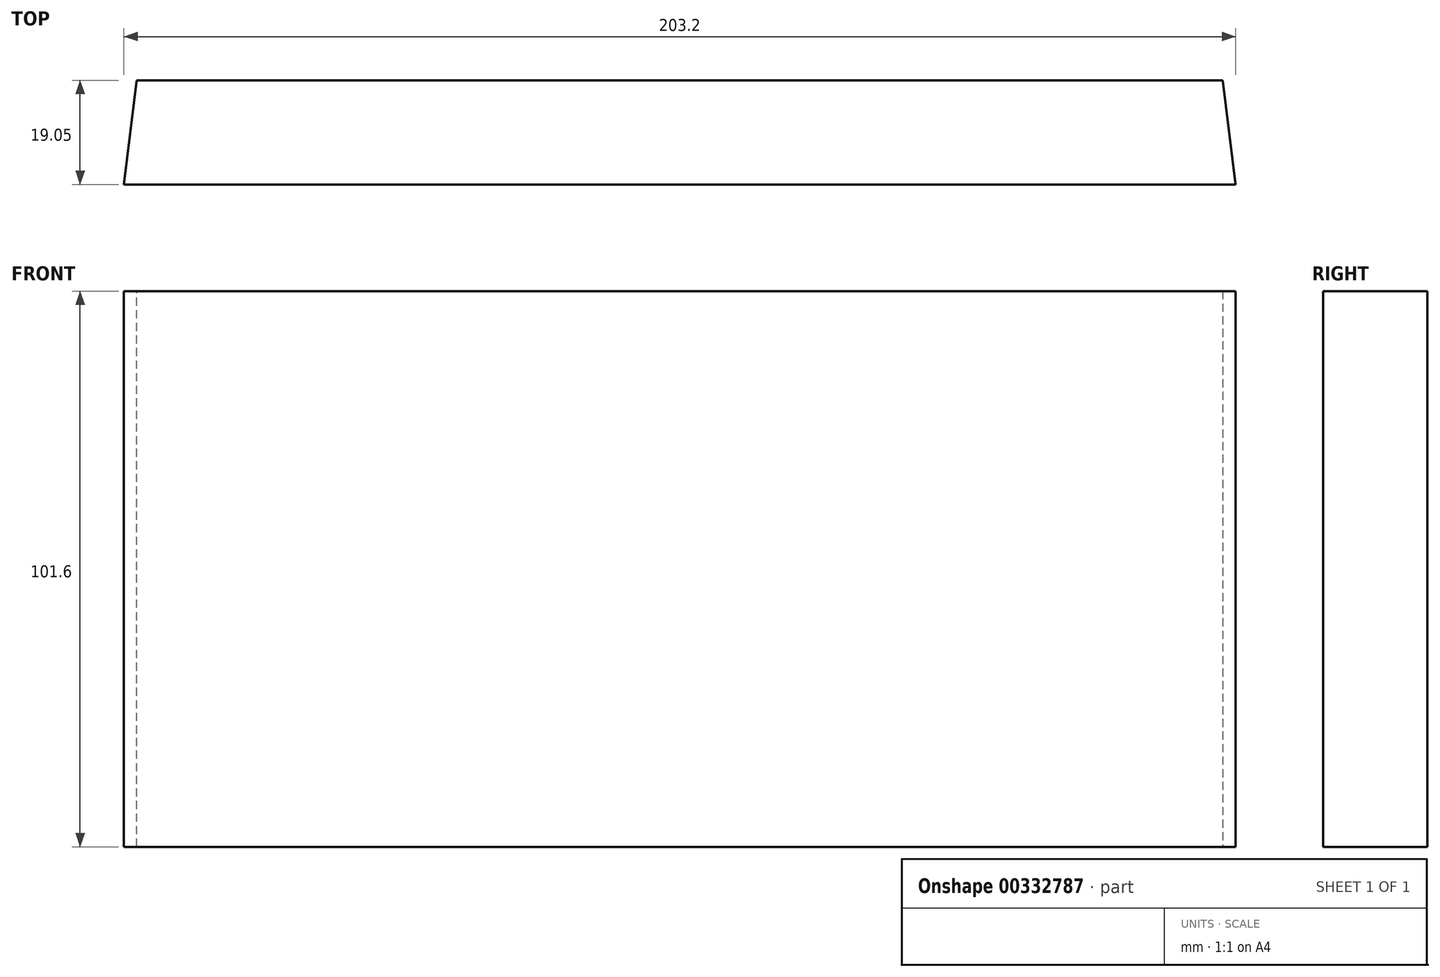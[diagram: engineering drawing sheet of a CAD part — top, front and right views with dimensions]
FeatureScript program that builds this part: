
annotation { "Feature Type Name" : "Feature", "Feature Type Description" : "" }
export const myFeature = defineFeature(function(context is Context, id is Id, definition is map)
    precondition{}
    {
        {
            var Q0;
            Q0=qCreatedBy(makeId("Front.planeOp"),FACE);
            var sketch = newSketch(context, id + "F0", { "sketchPlane" : qUnion([Q0])});
            skLineSegment(sketch, "E0.bottom", {"start": v(101.6, 50.8) * mm, "end": v(-101.6, 50.8) * mm});
            skLineSegment(sketch, "E0.top", {"start": v(101.6, -50.8) * mm, "end": v(-101.6, -50.8) * mm});
            skLineSegment(sketch, "E0.left", {"start": v(101.6, 50.8) * mm, "end": v(101.6, -50.8) * mm});
            skLineSegment(sketch, "E0.right", {"start": v(-101.6, 50.8) * mm, "end": v(-101.6, -50.8) * mm});
            skPoint(sketch, "E0.middle", {"position": v(0, 0) * mm});
            skSolve(sketch);
        }
        {
            var Q0;
            Q0=makeQuery(id+"F0.imprint","IMPRINT",FACE,{"disambiguationData":[TD([[makeQuery(id+"F0.imprint","IMPRINT",EDGE,{"derivedFrom":sQuery(id+"F0.wireOp",EDGE,"E0.bottom")}),1.0]])]});
            extrude(context, id + "F1", {"entities" : qUnion([Q0]), "depth" : 19.05 * mm});
        }
        {
            var Q0;
            Q0=makeQuery(id+"F1.opExtrude","CAP_EDGE",EDGE,{"disambiguationData":[OSD([sQuery(id+"F0.wireOp",EDGE,"E0.right")])],"isStart":true});
            chamfer(context, id + "F2", {"entities" : qUnion([Q0]), "chamferType" : ChamferType.OFFSET_ANGLE, "width" : 19.05 * mm, "oppositeDirection" : false, "angle" : 7 * degree, "tangentPropagation" : true});
        }
        {
            var Q0;
            Q0=makeQuery(id+"F1.opExtrude","CAP_EDGE",EDGE,{"disambiguationData":[OSD([sQuery(id+"F0.wireOp",EDGE,"E0.left")])],"isStart":true});
            chamfer(context, id + "F3", {"entities" : qUnion([Q0]), "chamferType" : ChamferType.OFFSET_ANGLE, "width" : 19.05 * mm, "oppositeDirection" : true, "angle" : 7 * degree, "tangentPropagation" : true});
        }
    });
